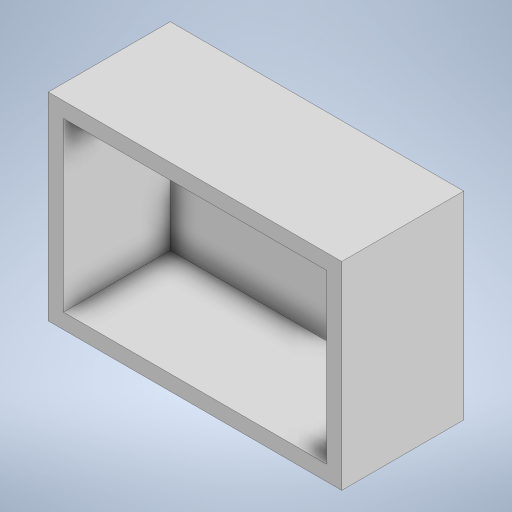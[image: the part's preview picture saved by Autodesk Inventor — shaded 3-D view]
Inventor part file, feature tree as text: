
AUTODESK INVENTOR PART (.ipt)
format: ipt  version: 2023 (Build 270158000, 158)  size: 194,048 bytes
history: native  units: mm
features: extrude x2, sketch x2
ambient origin geometry x8: Origin, YZ Plane, XZ Plane, XY Plane, X Axis, Y Axis, Z Axis, Center Point
bodies: Solid1 (feature_tree)
feature tree (4):
  extrude  "Extrusion1"  Depth=26.0mm
  extrude  "Extrusion2"  Depth=2.0mm
  sketch  "Sketch1"  dims[d0=38.5mm d1=26.0mm]
  sketch  "Sketch2"  dims[d2=16.0mm d3=0.0mm d4=2.0mm d5=2.0mm d6=2.0mm d7=2.0mm d8=14.0mm d9=0.0mm]
